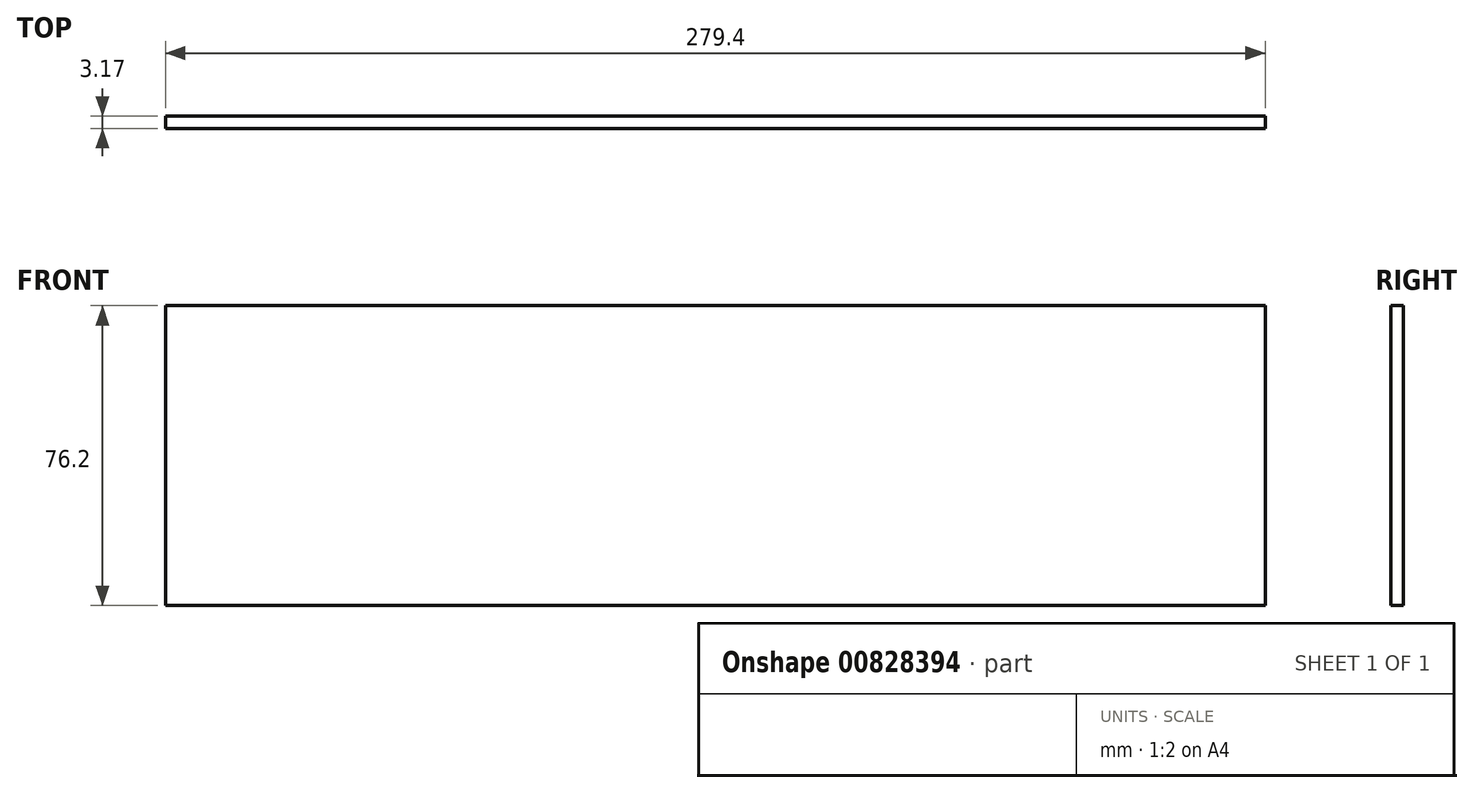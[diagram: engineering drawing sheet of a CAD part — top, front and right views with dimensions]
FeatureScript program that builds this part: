
annotation { "Feature Type Name" : "Feature", "Feature Type Description" : "" }
export const myFeature = defineFeature(function(context is Context, id is Id, definition is map)
    precondition{}
    {
        {
            var Q0;
            Q0=qCreatedBy(makeId("Front.planeOp"),FACE);
            var sketch = newSketch(context, id + "F0", { "sketchPlane" : qUnion([Q0])});
            skLineSegment(sketch, "E0.bottom", {"start": v(139.7, 38.1) * mm, "end": v(-139.7, 38.1) * mm});
            skLineSegment(sketch, "E0.top", {"start": v(139.7, -38.1) * mm, "end": v(-139.7, -38.1) * mm});
            skLineSegment(sketch, "E0.left", {"start": v(139.7, 38.1) * mm, "end": v(139.7, -38.1) * mm});
            skLineSegment(sketch, "E0.right", {"start": v(-139.7, 38.1) * mm, "end": v(-139.7, -38.1) * mm});
            skPoint(sketch, "E0.middle", {"position": v(0, 0) * mm});
            skSolve(sketch);
        }
        {
            var Q0;
            Q0 = qSketchRegion(id + "F0", true);
            extrude(context, id + "F1", {"entities" : qUnion([Q0]), "depth" : 3.17 * mm, "offsetDistance" : 25.4 * mm});
        }
    });
